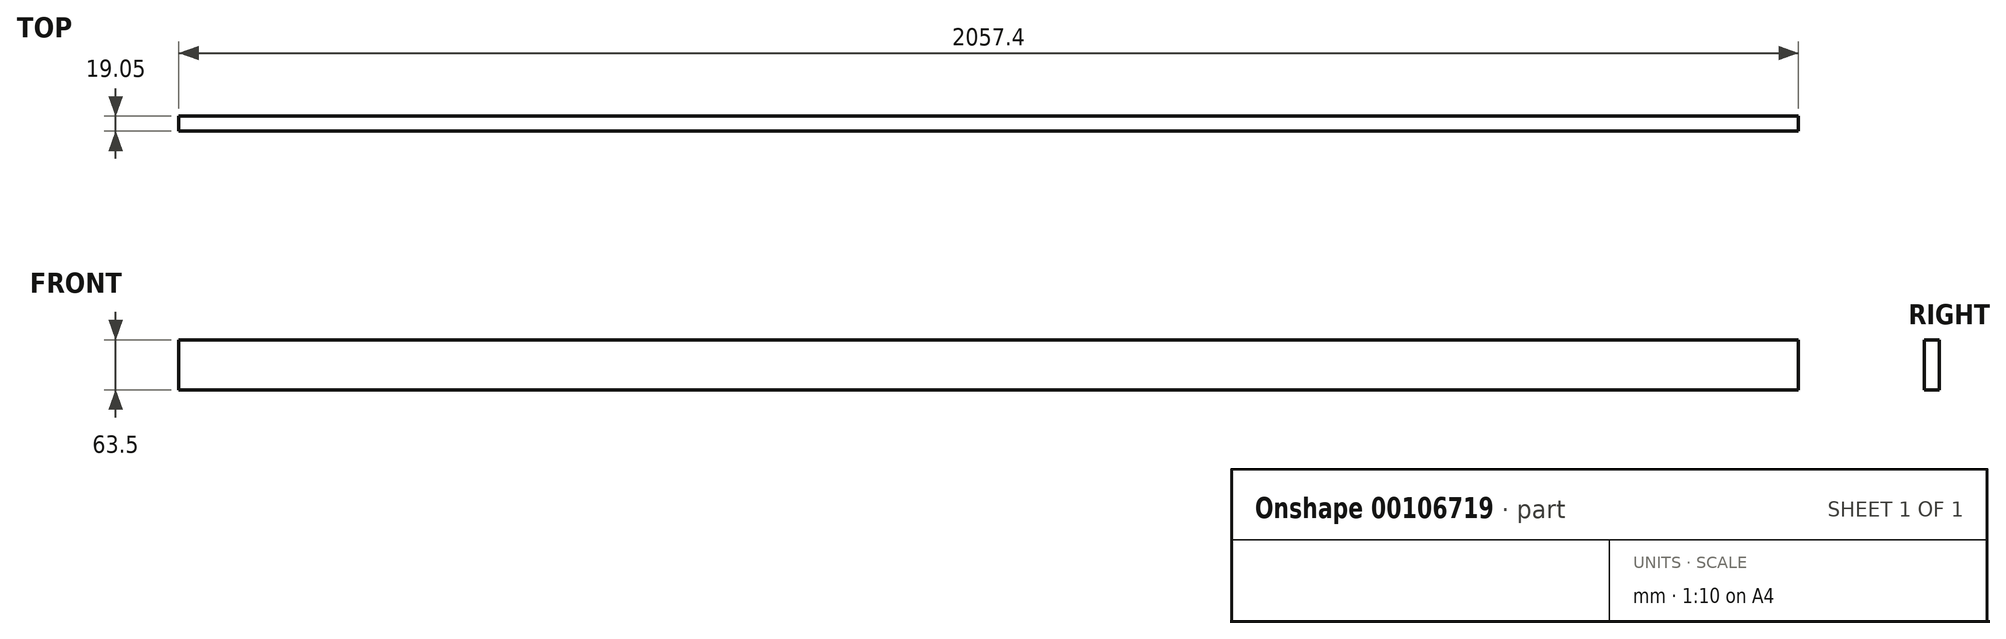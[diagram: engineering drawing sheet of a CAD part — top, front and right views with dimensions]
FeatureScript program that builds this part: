
annotation { "Feature Type Name" : "Feature", "Feature Type Description" : "" }
export const myFeature = defineFeature(function(context is Context, id is Id, definition is map)
    precondition{}
    {
        {
            var Q0;
            Q0=qCreatedBy(makeId("Front.planeOp"),FACE);
            var sketch = newSketch(context, id + "F0", { "sketchPlane" : qUnion([Q0])});
            skLineSegment(sketch, "E0.bottom", {"start": v(0, 0) * mm, "end": v(2057.4, 0) * mm});
            skLineSegment(sketch, "E0.top", {"start": v(0, 63.5) * mm, "end": v(2057.4, 63.5) * mm});
            skLineSegment(sketch, "E0.left", {"start": v(0, 0) * mm, "end": v(0, 63.5) * mm});
            skLineSegment(sketch, "E0.right", {"start": v(2057.4, 0) * mm, "end": v(2057.4, 63.5) * mm});
            skSolve(sketch);
        }
        {
            var Q0;
            Q0=makeQuery(id+"F0.imprint","IMPRINT",FACE,{"disambiguationData":[TD([[makeQuery(id+"F0.imprint","IMPRINT",EDGE,{"derivedFrom":sQuery(id+"F0.wireOp",EDGE,"E0.bottom")}),1.0]])]});
            extrude(context, id + "F1", {"entities" : qUnion([Q0]), "depth" : 19.05 * mm});
        }
    });
